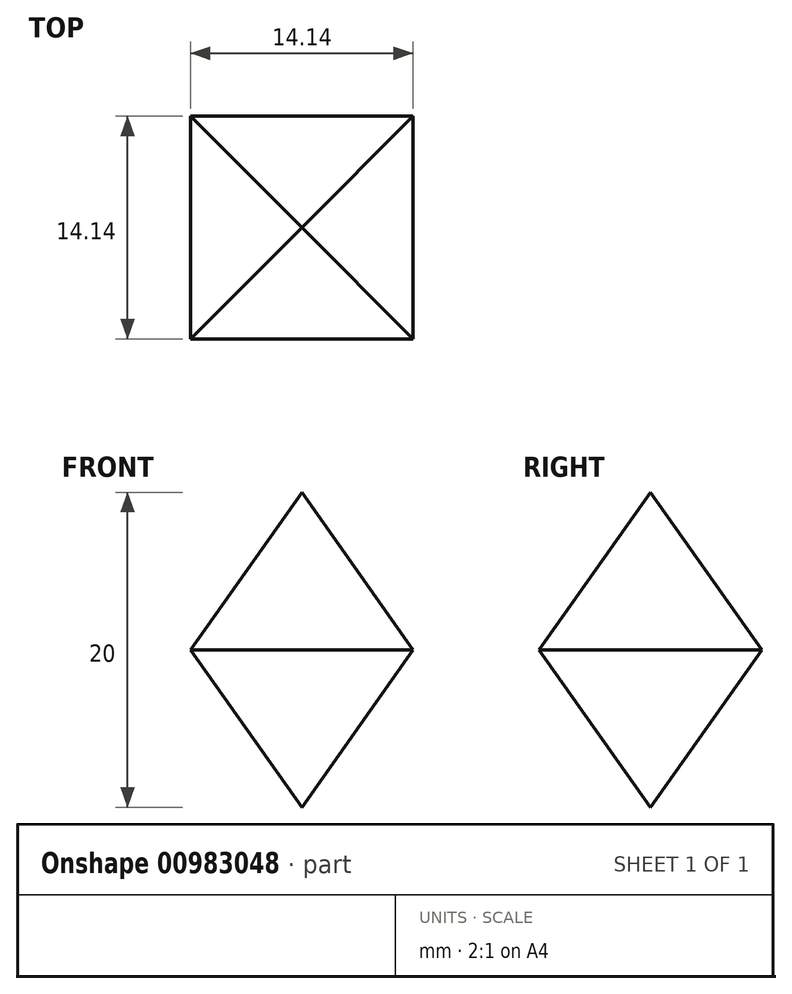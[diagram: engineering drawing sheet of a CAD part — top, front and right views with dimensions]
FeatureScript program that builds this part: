
annotation { "Feature Type Name" : "Feature", "Feature Type Description" : "" }
export const myFeature = defineFeature(function(context is Context, id is Id, definition is map)
    precondition{}
    {
        {
            var Q0;
            Q0=qCreatedBy(makeId("Top.planeOp"),FACE);
            var sketch = newSketch(context, id + "F0", { "sketchPlane" : qUnion([Q0])});
            skLineSegment(sketch, "E0.bottom", {"start": v(-7.07, 7.07) * mm, "end": v(7.07, 7.07) * mm});
            skLineSegment(sketch, "E0.top", {"start": v(-7.07, -7.07) * mm, "end": v(7.07, -7.07) * mm});
            skLineSegment(sketch, "E0.left", {"start": v(-7.07, 7.07) * mm, "end": v(-7.07, -7.07) * mm});
            skLineSegment(sketch, "E0.right", {"start": v(7.07, 7.07) * mm, "end": v(7.07, -7.07) * mm});
            skSolve(sketch);
        }
        {
            var Q0;
            Q0=makeQuery(id+"F0.imprint","IMPRINT",FACE,{"disambiguationData":[TD([[makeQuery(id+"F0.imprint","IMPRINT",EDGE,{"derivedFrom":sQuery(id+"F0.wireOp",EDGE,"E0.bottom")}),-1.0]])]});
            extrude(context, id + "F1", {"entities" : qUnion([Q0]), "offsetDistance" : 25 * mm, "depth" : 20 * mm, "hasDraft" : true, "draftAngle" : 35.26 * degree, "draftPullDirection" : true, "hasSecondDirection" : true, "secondDirectionOppositeDirection" : true, "secondDirectionDepth" : 20 * mm, "hasSecondDirectionDraft" : true, "secondDirectionDraftAngle" : 35.26 * degree, "secondDirectionDraftPullDirection" : true});
        }
    });
